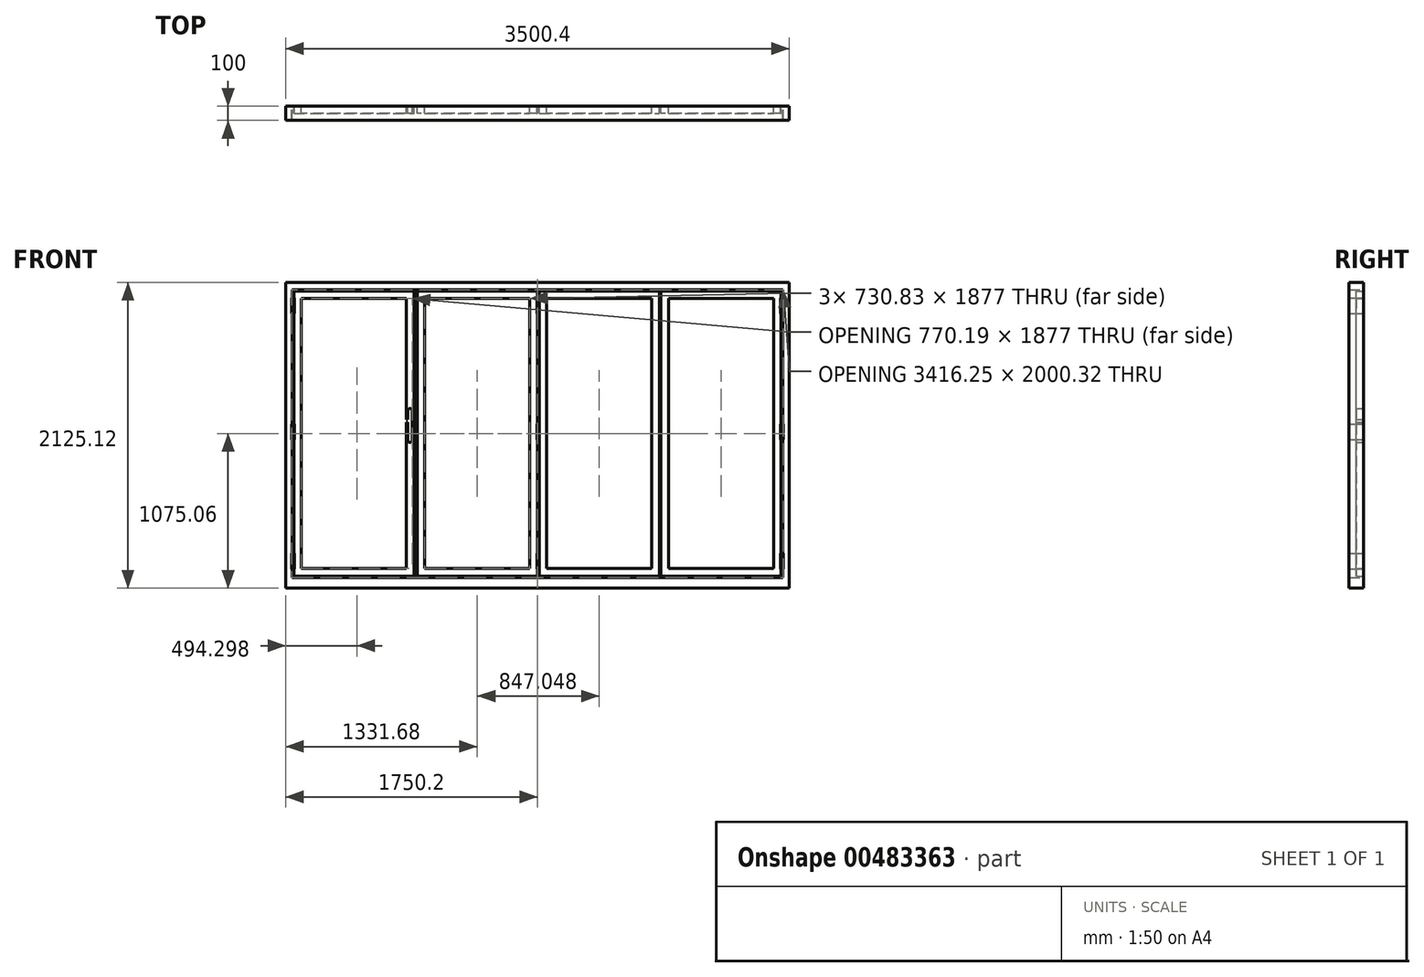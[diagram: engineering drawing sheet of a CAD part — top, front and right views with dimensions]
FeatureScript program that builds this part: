
annotation { "Feature Type Name" : "Feature", "Feature Type Description" : "" }
export const myFeature = defineFeature(function(context is Context, id is Id, definition is map)
    precondition{}
    {
        {
            var Q0;
            Q0=qCreatedBy(makeId("Front.planeOp"),FACE);
            var sketch = newSketch(context, id + "F0", { "sketchPlane" : qUnion([Q0])});
            skLineSegment(sketch, "E0", {"start": v(-1203.5, 497.7) * mm, "end": v(-1203.5, 547.7) * mm});
            skLineSegment(sketch, "E1", {"start": v(-1216.3, 497.7) * mm, "end": v(-1216.3, 547.7) * mm});
            skLineSegment(sketch, "E2", {"start": v(-1216.3, 497.7) * mm, "end": v(-1198.26, 497.7) * mm});
            skLineSegment(sketch, "E3", {"start": v(-1216.3, 547.7) * mm, "end": v(-1198.26, 547.7) * mm});
            skLineSegment(sketch, "E4", {"start": v(-1203.5, 551.7) * mm, "end": v(-1203.5, 601.7) * mm});
            skLineSegment(sketch, "E5", {"start": v(-1216.3, 551.7) * mm, "end": v(-1216.3, 601.7) * mm});
            skLineSegment(sketch, "E6", {"start": v(-1216.3, 551.7) * mm, "end": v(-1198.26, 551.7) * mm});
            skLineSegment(sketch, "E7", {"start": v(-1216.3, 601.7) * mm, "end": v(-1198.26, 601.7) * mm});
            skLineSegment(sketch, "E8", {"start": v(-1198.26, 547.7) * mm, "end": v(-1198.26, 549.7) * mm});
            skLineSegment(sketch, "E9", {"start": v(-1198.26, 549.7) * mm, "end": v(-1216.3, 549.7) * mm});
            skLineSegment(sketch, "E10", {"start": v(-1216.3, 549.7) * mm, "end": v(-1216.3, 547.7) * mm});
            skLineSegment(sketch, "E11", {"start": v(-1198.26, 551.7) * mm, "end": v(-1198.26, 549.7) * mm});
            skLineSegment(sketch, "E12", {"start": v(-1216.3, 549.7) * mm, "end": v(-1216.3, 551.7) * mm});
            skLineSegment(sketch, "E13", {"start": v(-1198.26, 497.7) * mm, "end": v(-1198.26, 495.7) * mm});
            skLineSegment(sketch, "E14", {"start": v(-1198.26, 495.7) * mm, "end": v(-1216.3, 495.7) * mm});
            skLineSegment(sketch, "E15", {"start": v(-1216.3, 495.7) * mm, "end": v(-1216.3, 497.7) * mm});
            skLineSegment(sketch, "E16", {"start": v(-1198.26, 601.7) * mm, "end": v(-1198.26, 603.7) * mm});
            skLineSegment(sketch, "E17", {"start": v(-1198.26, 603.7) * mm, "end": v(-1216.3, 603.7) * mm});
            skLineSegment(sketch, "E18", {"start": v(-1216.3, 603.7) * mm, "end": v(-1216.3, 601.7) * mm});
            skLineSegment(sketch, "E19", {"start": v(487.82, -378.21) * mm, "end": v(487.82, -328.21) * mm});
            skLineSegment(sketch, "E20", {"start": v(500.63, -378.21) * mm, "end": v(500.63, -328.21) * mm});
            skLineSegment(sketch, "E21", {"start": v(505.86, -378.21) * mm, "end": v(487.82, -378.21) * mm});
            skLineSegment(sketch, "E22", {"start": v(505.86, -328.21) * mm, "end": v(487.82, -328.21) * mm});
            skLineSegment(sketch, "E23", {"start": v(487.82, -324.21) * mm, "end": v(487.82, -274.21) * mm});
            skLineSegment(sketch, "E24", {"start": v(500.63, -324.21) * mm, "end": v(500.63, -274.21) * mm});
            skLineSegment(sketch, "E25", {"start": v(505.86, -324.21) * mm, "end": v(487.82, -324.21) * mm});
            skLineSegment(sketch, "E26", {"start": v(505.86, -274.21) * mm, "end": v(487.82, -274.21) * mm});
            skLineSegment(sketch, "E27", {"start": v(487.82, -328.21) * mm, "end": v(487.82, -326.21) * mm});
            skLineSegment(sketch, "E28", {"start": v(487.82, -326.21) * mm, "end": v(505.86, -326.21) * mm});
            skLineSegment(sketch, "E29", {"start": v(505.86, -326.21) * mm, "end": v(505.86, -328.21) * mm});
            skLineSegment(sketch, "E30", {"start": v(487.82, -324.21) * mm, "end": v(487.82, -326.21) * mm});
            skLineSegment(sketch, "E31", {"start": v(505.86, -326.21) * mm, "end": v(505.86, -324.21) * mm});
            skLineSegment(sketch, "E32", {"start": v(487.82, -378.21) * mm, "end": v(487.82, -380.21) * mm});
            skLineSegment(sketch, "E33", {"start": v(487.82, -380.21) * mm, "end": v(505.86, -380.21) * mm});
            skLineSegment(sketch, "E34", {"start": v(505.86, -380.21) * mm, "end": v(505.86, -378.21) * mm});
            skLineSegment(sketch, "E35", {"start": v(487.82, -274.21) * mm, "end": v(487.82, -272.21) * mm});
            skLineSegment(sketch, "E36", {"start": v(487.82, -272.21) * mm, "end": v(505.86, -272.21) * mm});
            skLineSegment(sketch, "E37", {"start": v(505.86, -272.21) * mm, "end": v(505.86, -274.21) * mm});
            skLineSegment(sketch, "E38", {"start": v(487.82, -1175.3) * mm, "end": v(487.82, -1225.3) * mm});
            skLineSegment(sketch, "E39", {"start": v(500.63, -1175.3) * mm, "end": v(500.63, -1225.3) * mm});
            skLineSegment(sketch, "E40", {"start": v(505.86, -1175.3) * mm, "end": v(487.82, -1175.3) * mm});
            skLineSegment(sketch, "E41", {"start": v(505.86, -1225.3) * mm, "end": v(487.82, -1225.3) * mm});
            skLineSegment(sketch, "E42", {"start": v(487.82, -1229.3) * mm, "end": v(487.82, -1279.3) * mm});
            skLineSegment(sketch, "E43", {"start": v(500.63, -1229.3) * mm, "end": v(500.63, -1279.3) * mm});
            skLineSegment(sketch, "E44", {"start": v(505.86, -1229.3) * mm, "end": v(487.82, -1229.3) * mm});
            skLineSegment(sketch, "E45", {"start": v(505.86, -1279.3) * mm, "end": v(487.82, -1279.3) * mm});
            skLineSegment(sketch, "E46", {"start": v(487.82, -1225.3) * mm, "end": v(487.82, -1227.3) * mm});
            skLineSegment(sketch, "E47", {"start": v(487.82, -1227.3) * mm, "end": v(505.86, -1227.3) * mm});
            skLineSegment(sketch, "E48", {"start": v(505.86, -1227.3) * mm, "end": v(505.86, -1225.3) * mm});
            skLineSegment(sketch, "E49", {"start": v(487.82, -1229.3) * mm, "end": v(487.82, -1227.3) * mm});
            skLineSegment(sketch, "E50", {"start": v(505.86, -1227.3) * mm, "end": v(505.86, -1229.3) * mm});
            skLineSegment(sketch, "E51", {"start": v(487.82, -1175.3) * mm, "end": v(487.82, -1173.3) * mm});
            skLineSegment(sketch, "E52", {"start": v(487.82, -1173.3) * mm, "end": v(505.86, -1173.3) * mm});
            skLineSegment(sketch, "E53", {"start": v(505.86, -1173.3) * mm, "end": v(505.86, -1175.3) * mm});
            skLineSegment(sketch, "E54", {"start": v(487.82, -1279.3) * mm, "end": v(487.82, -1281.3) * mm});
            skLineSegment(sketch, "E55", {"start": v(487.82, -1281.3) * mm, "end": v(505.86, -1281.3) * mm});
            skLineSegment(sketch, "E56", {"start": v(505.86, -1281.3) * mm, "end": v(505.86, -1279.3) * mm});
            skLineSegment(sketch, "E57", {"start": v(2181.92, -1175.3) * mm, "end": v(2181.92, -1225.3) * mm});
            skLineSegment(sketch, "E58", {"start": v(2199.95, -1175.3) * mm, "end": v(2199.95, -1225.3) * mm});
            skLineSegment(sketch, "E59", {"start": v(2199.95, -1175.3) * mm, "end": v(2181.92, -1175.3) * mm});
            skLineSegment(sketch, "E60", {"start": v(2199.95, -1225.3) * mm, "end": v(2181.92, -1225.3) * mm});
            skLineSegment(sketch, "E61", {"start": v(2181.92, -1229.3) * mm, "end": v(2181.92, -1279.3) * mm});
            skLineSegment(sketch, "E62", {"start": v(2199.95, -1229.3) * mm, "end": v(2199.95, -1279.3) * mm});
            skLineSegment(sketch, "E63", {"start": v(2199.95, -1229.3) * mm, "end": v(2181.92, -1229.3) * mm});
            skLineSegment(sketch, "E64", {"start": v(2199.95, -1279.3) * mm, "end": v(2181.92, -1279.3) * mm});
            skLineSegment(sketch, "E65", {"start": v(2181.92, -1225.3) * mm, "end": v(2181.92, -1227.3) * mm});
            skLineSegment(sketch, "E66", {"start": v(2181.92, -1227.3) * mm, "end": v(2199.95, -1227.3) * mm});
            skLineSegment(sketch, "E67", {"start": v(2199.95, -1227.3) * mm, "end": v(2199.95, -1225.3) * mm});
            skLineSegment(sketch, "E68", {"start": v(2181.92, -1229.3) * mm, "end": v(2181.92, -1227.3) * mm});
            skLineSegment(sketch, "E69", {"start": v(2199.95, -1227.3) * mm, "end": v(2199.95, -1229.3) * mm});
            skLineSegment(sketch, "E70", {"start": v(2181.92, -1175.3) * mm, "end": v(2181.92, -1173.3) * mm});
            skLineSegment(sketch, "E71", {"start": v(2181.92, -1173.3) * mm, "end": v(2199.95, -1173.3) * mm});
            skLineSegment(sketch, "E72", {"start": v(2199.95, -1173.3) * mm, "end": v(2199.95, -1175.3) * mm});
            skLineSegment(sketch, "E73", {"start": v(2181.92, -1279.3) * mm, "end": v(2181.92, -1281.3) * mm});
            skLineSegment(sketch, "E74", {"start": v(2181.92, -1281.3) * mm, "end": v(2199.95, -1281.3) * mm});
            skLineSegment(sketch, "E75", {"start": v(2199.95, -1281.3) * mm, "end": v(2199.95, -1279.3) * mm});
            skLineSegment(sketch, "E76", {"start": v(2181.92, -378.21) * mm, "end": v(2181.92, -328.21) * mm});
            skLineSegment(sketch, "E77", {"start": v(2199.95, -378.21) * mm, "end": v(2199.95, -328.21) * mm});
            skLineSegment(sketch, "E78", {"start": v(2199.95, -378.21) * mm, "end": v(2181.92, -378.21) * mm});
            skLineSegment(sketch, "E79", {"start": v(2199.95, -328.21) * mm, "end": v(2181.92, -328.21) * mm});
            skLineSegment(sketch, "E80", {"start": v(2181.92, -324.21) * mm, "end": v(2181.92, -274.21) * mm});
            skLineSegment(sketch, "E81", {"start": v(2199.95, -324.21) * mm, "end": v(2199.95, -274.21) * mm});
            skLineSegment(sketch, "E82", {"start": v(2199.95, -324.21) * mm, "end": v(2181.92, -324.21) * mm});
            skLineSegment(sketch, "E83", {"start": v(2199.95, -274.21) * mm, "end": v(2181.92, -274.21) * mm});
            skLineSegment(sketch, "E84", {"start": v(2181.92, -328.21) * mm, "end": v(2181.92, -326.21) * mm});
            skLineSegment(sketch, "E85", {"start": v(2181.92, -326.21) * mm, "end": v(2199.95, -326.21) * mm});
            skLineSegment(sketch, "E86", {"start": v(2199.95, -326.21) * mm, "end": v(2199.95, -328.21) * mm});
            skLineSegment(sketch, "E87", {"start": v(2181.92, -324.21) * mm, "end": v(2181.92, -326.21) * mm});
            skLineSegment(sketch, "E88", {"start": v(2199.95, -326.21) * mm, "end": v(2199.95, -324.21) * mm});
            skLineSegment(sketch, "E89", {"start": v(2181.92, -378.21) * mm, "end": v(2181.92, -380.21) * mm});
            skLineSegment(sketch, "E90", {"start": v(2181.92, -380.21) * mm, "end": v(2199.95, -380.21) * mm});
            skLineSegment(sketch, "E91", {"start": v(2199.95, -380.21) * mm, "end": v(2199.95, -378.21) * mm});
            skLineSegment(sketch, "E92", {"start": v(2181.92, -274.21) * mm, "end": v(2181.92, -272.21) * mm});
            skLineSegment(sketch, "E93", {"start": v(2181.92, -272.21) * mm, "end": v(2199.95, -272.21) * mm});
            skLineSegment(sketch, "E94", {"start": v(2199.95, -272.21) * mm, "end": v(2199.95, -274.21) * mm});
            skLineSegment(sketch, "E95", {"start": v(2181.92, 497.7) * mm, "end": v(2181.92, 547.7) * mm});
            skLineSegment(sketch, "E96", {"start": v(2199.95, 497.7) * mm, "end": v(2199.95, 547.7) * mm});
            skLineSegment(sketch, "E97", {"start": v(2199.95, 497.7) * mm, "end": v(2181.92, 497.7) * mm});
            skLineSegment(sketch, "E98", {"start": v(2199.95, 547.7) * mm, "end": v(2181.92, 547.7) * mm});
            skLineSegment(sketch, "E99", {"start": v(2181.92, 551.7) * mm, "end": v(2181.92, 601.7) * mm});
            skLineSegment(sketch, "E100", {"start": v(2199.95, 551.7) * mm, "end": v(2199.95, 601.7) * mm});
            skLineSegment(sketch, "E101", {"start": v(2199.95, 551.7) * mm, "end": v(2181.92, 551.7) * mm});
            skLineSegment(sketch, "E102", {"start": v(2199.95, 601.7) * mm, "end": v(2181.92, 601.7) * mm});
            skLineSegment(sketch, "E103", {"start": v(2181.92, 547.7) * mm, "end": v(2181.92, 549.7) * mm});
            skLineSegment(sketch, "E104", {"start": v(2181.92, 549.7) * mm, "end": v(2199.95, 549.7) * mm});
            skLineSegment(sketch, "E105", {"start": v(2199.95, 549.7) * mm, "end": v(2199.95, 547.7) * mm});
            skLineSegment(sketch, "E106", {"start": v(2181.92, 551.7) * mm, "end": v(2181.92, 549.7) * mm});
            skLineSegment(sketch, "E107", {"start": v(2199.95, 549.7) * mm, "end": v(2199.95, 551.7) * mm});
            skLineSegment(sketch, "E108", {"start": v(2181.92, 497.7) * mm, "end": v(2181.92, 495.7) * mm});
            skLineSegment(sketch, "E109", {"start": v(2181.92, 495.7) * mm, "end": v(2199.95, 495.7) * mm});
            skLineSegment(sketch, "E110", {"start": v(2199.95, 495.7) * mm, "end": v(2199.95, 497.7) * mm});
            skLineSegment(sketch, "E111", {"start": v(2181.92, 601.7) * mm, "end": v(2181.92, 603.7) * mm});
            skLineSegment(sketch, "E112", {"start": v(2181.92, 603.7) * mm, "end": v(2199.95, 603.7) * mm});
            skLineSegment(sketch, "E113", {"start": v(2199.95, 603.7) * mm, "end": v(2199.95, 601.7) * mm});
            skLineSegment(sketch, "E114", {"start": v(-1203.5, -378.21) * mm, "end": v(-1203.5, -328.21) * mm});
            skLineSegment(sketch, "E115", {"start": v(-1216.3, -378.21) * mm, "end": v(-1216.3, -328.21) * mm});
            skLineSegment(sketch, "E116", {"start": v(-1216.3, -378.21) * mm, "end": v(-1198.26, -378.21) * mm});
            skLineSegment(sketch, "E117", {"start": v(-1216.3, -328.21) * mm, "end": v(-1198.26, -328.21) * mm});
            skLineSegment(sketch, "E118", {"start": v(-1203.5, -324.21) * mm, "end": v(-1203.5, -274.21) * mm});
            skLineSegment(sketch, "E119", {"start": v(-1216.3, -324.21) * mm, "end": v(-1216.3, -274.21) * mm});
            skLineSegment(sketch, "E120", {"start": v(-1216.3, -324.21) * mm, "end": v(-1198.26, -324.21) * mm});
            skLineSegment(sketch, "E121", {"start": v(-1216.3, -274.21) * mm, "end": v(-1198.26, -274.21) * mm});
            skLineSegment(sketch, "E122", {"start": v(-1198.26, -328.21) * mm, "end": v(-1198.26, -326.21) * mm});
            skLineSegment(sketch, "E123", {"start": v(-1198.26, -326.21) * mm, "end": v(-1216.3, -326.21) * mm});
            skLineSegment(sketch, "E124", {"start": v(-1216.3, -326.21) * mm, "end": v(-1216.3, -328.21) * mm});
            skLineSegment(sketch, "E125", {"start": v(-1198.26, -324.21) * mm, "end": v(-1198.26, -326.21) * mm});
            skLineSegment(sketch, "E126", {"start": v(-1216.3, -326.21) * mm, "end": v(-1216.3, -324.21) * mm});
            skLineSegment(sketch, "E127", {"start": v(-1198.26, -378.21) * mm, "end": v(-1198.26, -380.21) * mm});
            skLineSegment(sketch, "E128", {"start": v(-1198.26, -380.21) * mm, "end": v(-1216.3, -380.21) * mm});
            skLineSegment(sketch, "E129", {"start": v(-1216.3, -380.21) * mm, "end": v(-1216.3, -378.21) * mm});
            skLineSegment(sketch, "E130", {"start": v(-1198.26, -274.21) * mm, "end": v(-1198.26, -272.21) * mm});
            skLineSegment(sketch, "E131", {"start": v(-1198.26, -272.21) * mm, "end": v(-1216.3, -272.21) * mm});
            skLineSegment(sketch, "E132", {"start": v(-1216.3, -272.21) * mm, "end": v(-1216.3, -274.21) * mm});
            skLineSegment(sketch, "E133", {"start": v(-1203.5, -1175.3) * mm, "end": v(-1203.5, -1225.3) * mm});
            skLineSegment(sketch, "E134", {"start": v(-1216.3, -1175.3) * mm, "end": v(-1216.3, -1225.3) * mm});
            skLineSegment(sketch, "E135", {"start": v(-1216.3, -1175.3) * mm, "end": v(-1198.26, -1175.3) * mm});
            skLineSegment(sketch, "E136", {"start": v(-1216.3, -1225.3) * mm, "end": v(-1198.26, -1225.3) * mm});
            skLineSegment(sketch, "E137", {"start": v(-1203.5, -1229.3) * mm, "end": v(-1203.5, -1279.3) * mm});
            skLineSegment(sketch, "E138", {"start": v(-1216.3, -1229.3) * mm, "end": v(-1216.3, -1279.3) * mm});
            skLineSegment(sketch, "E139", {"start": v(-1216.3, -1229.3) * mm, "end": v(-1198.26, -1229.3) * mm});
            skLineSegment(sketch, "E140", {"start": v(-1216.3, -1279.3) * mm, "end": v(-1198.26, -1279.3) * mm});
            skLineSegment(sketch, "E141", {"start": v(-1198.26, -1225.3) * mm, "end": v(-1198.26, -1227.3) * mm});
            skLineSegment(sketch, "E142", {"start": v(-1198.26, -1227.3) * mm, "end": v(-1216.3, -1227.3) * mm});
            skLineSegment(sketch, "E143", {"start": v(-1216.3, -1227.3) * mm, "end": v(-1216.3, -1225.3) * mm});
            skLineSegment(sketch, "E144", {"start": v(-1198.26, -1229.3) * mm, "end": v(-1198.26, -1227.3) * mm});
            skLineSegment(sketch, "E145", {"start": v(-1216.3, -1227.3) * mm, "end": v(-1216.3, -1229.3) * mm});
            skLineSegment(sketch, "E146", {"start": v(-1198.26, -1175.3) * mm, "end": v(-1198.26, -1173.3) * mm});
            skLineSegment(sketch, "E147", {"start": v(-1198.26, -1173.3) * mm, "end": v(-1216.3, -1173.3) * mm});
            skLineSegment(sketch, "E148", {"start": v(-1216.3, -1173.3) * mm, "end": v(-1216.3, -1175.3) * mm});
            skLineSegment(sketch, "E149", {"start": v(-1198.26, -1279.3) * mm, "end": v(-1198.26, -1281.3) * mm});
            skLineSegment(sketch, "E150", {"start": v(-1198.26, -1281.3) * mm, "end": v(-1216.3, -1281.3) * mm});
            skLineSegment(sketch, "E151", {"start": v(-1216.3, -1281.3) * mm, "end": v(-1216.3, -1279.3) * mm});
            skLineSegment(sketch, "E152", {"start": v(487.82, 497.7) * mm, "end": v(487.82, 547.7) * mm});
            skLineSegment(sketch, "E153", {"start": v(500.63, 497.7) * mm, "end": v(500.63, 547.7) * mm});
            skLineSegment(sketch, "E154", {"start": v(505.86, 497.7) * mm, "end": v(487.82, 497.7) * mm});
            skLineSegment(sketch, "E155", {"start": v(505.86, 547.7) * mm, "end": v(487.82, 547.7) * mm});
            skLineSegment(sketch, "E156", {"start": v(487.82, 551.7) * mm, "end": v(487.82, 601.7) * mm});
            skLineSegment(sketch, "E157", {"start": v(500.63, 551.7) * mm, "end": v(500.63, 601.7) * mm});
            skLineSegment(sketch, "E158", {"start": v(505.86, 551.7) * mm, "end": v(487.82, 551.7) * mm});
            skLineSegment(sketch, "E159", {"start": v(505.86, 601.7) * mm, "end": v(487.82, 601.7) * mm});
            skLineSegment(sketch, "E160", {"start": v(487.82, 547.7) * mm, "end": v(487.82, 549.7) * mm});
            skLineSegment(sketch, "E161", {"start": v(487.82, 549.7) * mm, "end": v(505.86, 549.7) * mm});
            skLineSegment(sketch, "E162", {"start": v(505.86, 549.7) * mm, "end": v(505.86, 547.7) * mm});
            skLineSegment(sketch, "E163", {"start": v(487.82, 551.7) * mm, "end": v(487.82, 549.7) * mm});
            skLineSegment(sketch, "E164", {"start": v(505.86, 549.7) * mm, "end": v(505.86, 551.7) * mm});
            skLineSegment(sketch, "E165", {"start": v(487.82, 497.7) * mm, "end": v(487.82, 495.7) * mm});
            skLineSegment(sketch, "E166", {"start": v(487.82, 495.7) * mm, "end": v(505.86, 495.7) * mm});
            skLineSegment(sketch, "E167", {"start": v(505.86, 495.7) * mm, "end": v(505.86, 497.7) * mm});
            skLineSegment(sketch, "E168", {"start": v(487.82, 601.7) * mm, "end": v(487.82, 603.7) * mm});
            skLineSegment(sketch, "E169", {"start": v(487.82, 603.7) * mm, "end": v(505.86, 603.7) * mm});
            skLineSegment(sketch, "E170", {"start": v(505.86, 603.7) * mm, "end": v(505.86, 601.7) * mm});
            skLineSegment(sketch, "E171", {"start": v(2196.94, -380.21) * mm, "end": v(2196.94, -1173.3) * mm});
            skLineSegment(sketch, "E172", {"start": v(2242.03, -1329.3) * mm, "end": v(2242.03, -1017.31) * mm});
            skLineSegment(sketch, "E173", {"start": v(2196.94, -1329.3) * mm, "end": v(2196.94, -1338.95) * mm});
            skLineSegment(sketch, "E174", {"start": v(-344.2, -1329.3) * mm, "end": v(-363.24, -1329.3) * mm});
            skLineSegment(sketch, "E175", {"start": v(-1137.64, -1265.8) * mm, "end": v(-429.86, -1265.8) * mm});
            skLineSegment(sketch, "E176", {"start": v(-1124.75, -1252.92) * mm, "end": v(-1201.27, -1329.3) * mm});
            skLineSegment(sketch, "E177", {"start": v(-1201.27, -380.21) * mm, "end": v(-1201.27, -1173.3) * mm});
            skLineSegment(sketch, "E178", {"start": v(-1213.29, -1281.3) * mm, "end": v(-1213.29, -1329.3) * mm});
            skLineSegment(sketch, "E179", {"start": v(-1213.29, -380.21) * mm, "end": v(-1213.29, -1173.3) * mm});
            skLineSegment(sketch, "E180", {"start": v(-1201.27, -1281.3) * mm, "end": v(-1201.27, -1329.3) * mm});
            skLineSegment(sketch, "E181", {"start": v(-1201.27, -1329.3) * mm, "end": v(-366.24, -1329.3) * mm});
            skLineSegment(sketch, "E182", {"start": v(-418.34, -1277.3) * mm, "end": v(-1149.17, -1277.3) * mm});
            skLineSegment(sketch, "E183", {"start": v(-438.73, -1256.94) * mm, "end": v(-1128.77, -1256.94) * mm});
            skLineSegment(sketch, "E184", {"start": v(-442.76, -1252.92) * mm, "end": v(-366.24, -1329.3) * mm});
            skLineSegment(sketch, "E185", {"start": v(-366.24, -1017.31) * mm, "end": v(-366.24, -1329.3) * mm});
            skLineSegment(sketch, "E186", {"start": v(-442.76, -1252.92) * mm, "end": v(-1124.75, -1252.92) * mm});
            skLineSegment(sketch, "E187", {"start": v(-1258.37, -1388.85) * mm, "end": v(-1258.37, -1338.95) * mm});
            skLineSegment(sketch, "E188", {"start": v(-1213.29, -1329.3) * mm, "end": v(-1213.29, -1338.95) * mm});
            skLineSegment(sketch, "E189", {"start": v(2196.94, -272.21) * mm, "end": v(2196.94, 495.7) * mm});
            skLineSegment(sketch, "E190", {"start": v(2242.03, 651.7) * mm, "end": v(2242.03, -1084.15) * mm});
            skLineSegment(sketch, "E191", {"start": v(2196.94, 651.7) * mm, "end": v(2196.94, 661.36) * mm});
            skLineSegment(sketch, "E192", {"start": v(-363.24, 651.7) * mm, "end": v(-363.24, -1329.3) * mm});
            skLineSegment(sketch, "E193", {"start": v(-344.2, 651.7) * mm, "end": v(-363.24, 651.7) * mm});
            skLineSegment(sketch, "E194", {"start": v(-1149.17, -1277.3) * mm, "end": v(-1149.17, 599.7) * mm});
            skLineSegment(sketch, "E195", {"start": v(-1137.64, -1265.8) * mm, "end": v(-1137.64, 588.2) * mm});
            skLineSegment(sketch, "E196", {"start": v(-1128.77, -1256.94) * mm, "end": v(-1128.77, 579.35) * mm});
            skLineSegment(sketch, "E197", {"start": v(-1124.75, 575.34) * mm, "end": v(-1201.27, 651.7) * mm});
            skLineSegment(sketch, "E198", {"start": v(-1201.27, -272.21) * mm, "end": v(-1201.27, 495.7) * mm});
            skLineSegment(sketch, "E199", {"start": v(-1213.29, 603.7) * mm, "end": v(-1213.29, 651.7) * mm});
            skLineSegment(sketch, "E200", {"start": v(-1213.29, -272.21) * mm, "end": v(-1213.29, 495.7) * mm});
            skLineSegment(sketch, "E201", {"start": v(-1124.75, -1252.92) * mm, "end": v(-1124.75, 575.34) * mm});
            skLineSegment(sketch, "E202", {"start": v(-1201.27, 603.7) * mm, "end": v(-1201.27, 651.7) * mm});
            skLineSegment(sketch, "E203", {"start": v(-1201.27, 651.7) * mm, "end": v(-366.24, 651.7) * mm});
            skLineSegment(sketch, "E204", {"start": v(-418.34, 599.7) * mm, "end": v(-1149.17, 599.7) * mm});
            skLineSegment(sketch, "E205", {"start": v(-429.86, 588.2) * mm, "end": v(-1137.64, 588.2) * mm});
            skLineSegment(sketch, "E206", {"start": v(-438.73, 579.35) * mm, "end": v(-1128.77, 579.35) * mm});
            skLineSegment(sketch, "E207", {"start": v(-442.76, 575.34) * mm, "end": v(-366.24, 651.7) * mm});
            skLineSegment(sketch, "E208", {"start": v(-366.24, -1084.15) * mm, "end": v(-366.24, 651.7) * mm});
            skLineSegment(sketch, "E209", {"start": v(-442.76, 575.34) * mm, "end": v(-1124.75, 575.34) * mm});
            skLineSegment(sketch, "E210", {"start": v(-1213.29, 651.7) * mm, "end": v(-1213.29, 661.36) * mm});
            skArc(sketch, "E211", {"start": v(-385.44, -247.83) * mm, "mid": v(-386.91, -244.3) * mm, "end": v(-390.45, -242.83) * mm});
            skLineSegment(sketch, "E212", {"start": v(-390.45, -242.83) * mm, "end": v(-497.12, -242.83) * mm});
            skArc(sketch, "E213", {"start": v(-497.12, -242.83) * mm, "mid": v(-504.2, -245.75) * mm, "end": v(-507.14, -252.83) * mm});
            skLineSegment(sketch, "E214", {"start": v(-507.14, -252.83) * mm, "end": v(-507.14, -251.52) * mm});
            skArc(sketch, "E215", {"start": v(-507.14, -251.52) * mm, "mid": v(-504.2, -258.6) * mm, "end": v(-497.12, -261.52) * mm});
            skLineSegment(sketch, "E216", {"start": v(-497.12, -261.52) * mm, "end": v(-390.45, -261.52) * mm});
            skArc(sketch, "E217", {"start": v(-390.45, -261.52) * mm, "mid": v(-386.91, -260.06) * mm, "end": v(-385.44, -256.52) * mm});
            skLineSegment(sketch, "E218", {"start": v(-385.44, -256.52) * mm, "end": v(-385.44, -247.83) * mm});
            skLineSegment(sketch, "E219", {"start": v(-410.04, -261.52) * mm, "end": v(-410.04, -385.57) * mm});
            skArc(sketch, "E220", {"start": v(-410.04, -385.57) * mm, "mid": v(-405.48, -396.54) * mm, "end": v(-394.5, -401.07) * mm});
            skArc(sketch, "E221", {"start": v(-394.5, -401.07) * mm, "mid": v(-383.53, -396.54) * mm, "end": v(-378.98, -385.57) * mm});
            skLineSegment(sketch, "E222", {"start": v(-378.98, -385.57) * mm, "end": v(-378.98, -181.57) * mm});
            skArc(sketch, "E223", {"start": v(-378.98, -181.57) * mm, "mid": v(-383.53, -170.6) * mm, "end": v(-394.5, -166.07) * mm});
            skArc(sketch, "E224", {"start": v(-394.5, -166.07) * mm, "mid": v(-405.48, -170.6) * mm, "end": v(-410.04, -181.57) * mm});
            skLineSegment(sketch, "E225", {"start": v(-410.04, -181.57) * mm, "end": v(-410.04, -242.83) * mm});
            skLineSegment(sketch, "E226", {"start": v(-399.52, -349.8) * mm, "end": v(-399.52, -361.78) * mm});
            skLineSegment(sketch, "E227", {"start": v(-389.5, -361.78) * mm, "end": v(-389.5, -349.8) * mm});
            skLineSegment(sketch, "E228", {"start": v(-442.76, -1252.92) * mm, "end": v(-442.76, -261.52) * mm});
            skLineSegment(sketch, "E229", {"start": v(-442.76, -242.83) * mm, "end": v(-442.76, 575.34) * mm});
            skLineSegment(sketch, "E230", {"start": v(-438.73, -242.83) * mm, "end": v(-438.73, 579.35) * mm});
            skLineSegment(sketch, "E231", {"start": v(-438.73, -1256.94) * mm, "end": v(-438.73, -261.52) * mm});
            skLineSegment(sketch, "E232", {"start": v(-429.86, -242.83) * mm, "end": v(-429.86, 588.2) * mm});
            skLineSegment(sketch, "E233", {"start": v(-429.86, -1265.8) * mm, "end": v(-429.86, -261.52) * mm});
            skLineSegment(sketch, "E234", {"start": v(-418.34, -242.83) * mm, "end": v(-418.34, 599.7) * mm});
            skLineSegment(sketch, "E235", {"start": v(-418.34, -1277.3) * mm, "end": v(-418.34, -261.52) * mm});
            skArc(sketch, "E236", {"start": v(-399.52, -361.78) * mm, "mid": v(-398.05, -365.32) * mm, "end": v(-394.5, -366.79) * mm});
            skArc(sketch, "E237", {"start": v(-394.5, -366.79) * mm, "mid": v(-390.97, -365.32) * mm, "end": v(-389.5, -361.78) * mm});
            skArc(sketch, "E238", {"start": v(-389.5, -349.82) * mm, "mid": v(-394.5, -334.42) * mm, "end": v(-399.52, -349.82) * mm});
            skLineSegment(sketch, "E239", {"start": v(427.2, -1265.8) * mm, "end": v(-280.58, -1265.8) * mm});
            skLineSegment(sketch, "E240", {"start": v(414.3, -1252.92) * mm, "end": v(490.83, -1329.3) * mm});
            skLineSegment(sketch, "E241", {"start": v(490.83, -380.21) * mm, "end": v(490.83, -1173.3) * mm});
            skLineSegment(sketch, "E242", {"start": v(490.83, -1281.3) * mm, "end": v(490.83, -1329.3) * mm});
            skLineSegment(sketch, "E243", {"start": v(490.83, -1329.3) * mm, "end": v(-344.2, -1329.3) * mm});
            skLineSegment(sketch, "E244", {"start": v(-292.1, -1277.3) * mm, "end": v(438.73, -1277.3) * mm});
            skLineSegment(sketch, "E245", {"start": v(-271.7, -1256.94) * mm, "end": v(418.33, -1256.94) * mm});
            skLineSegment(sketch, "E246", {"start": v(-267.68, -1252.92) * mm, "end": v(-344.2, -1329.3) * mm});
            skLineSegment(sketch, "E247", {"start": v(-344.2, -1017.31) * mm, "end": v(-344.2, -1173.3) * mm});
            skLineSegment(sketch, "E248", {"start": v(-267.68, -1252.92) * mm, "end": v(414.3, -1252.92) * mm});
            skLineSegment(sketch, "E249", {"start": v(438.73, -1277.3) * mm, "end": v(438.73, 599.7) * mm});
            skLineSegment(sketch, "E250", {"start": v(427.2, -1265.8) * mm, "end": v(427.2, 588.2) * mm});
            skLineSegment(sketch, "E251", {"start": v(418.33, -1256.94) * mm, "end": v(418.33, 579.35) * mm});
            skLineSegment(sketch, "E252", {"start": v(414.3, 575.34) * mm, "end": v(490.83, 651.7) * mm});
            skLineSegment(sketch, "E253", {"start": v(490.83, -272.21) * mm, "end": v(490.83, 495.7) * mm});
            skLineSegment(sketch, "E254", {"start": v(414.3, -1252.92) * mm, "end": v(414.3, 575.34) * mm});
            skLineSegment(sketch, "E255", {"start": v(490.83, 603.7) * mm, "end": v(490.83, 651.7) * mm});
            skLineSegment(sketch, "E256", {"start": v(490.83, 651.7) * mm, "end": v(-344.2, 651.7) * mm});
            skLineSegment(sketch, "E257", {"start": v(-292.1, 599.7) * mm, "end": v(438.73, 599.7) * mm});
            skLineSegment(sketch, "E258", {"start": v(-280.58, 588.2) * mm, "end": v(427.2, 588.2) * mm});
            skLineSegment(sketch, "E259", {"start": v(-271.7, 579.35) * mm, "end": v(418.33, 579.35) * mm});
            skLineSegment(sketch, "E260", {"start": v(-267.68, 575.34) * mm, "end": v(-344.2, 651.7) * mm});
            skLineSegment(sketch, "E261", {"start": v(-344.2, -1329.3) * mm, "end": v(-344.2, 651.7) * mm});
            skLineSegment(sketch, "E262", {"start": v(-267.68, 575.34) * mm, "end": v(414.3, 575.34) * mm});
            skLineSegment(sketch, "E263", {"start": v(-267.68, -1252.92) * mm, "end": v(-267.68, 575.34) * mm});
            skLineSegment(sketch, "E264", {"start": v(-271.7, -1256.94) * mm, "end": v(-271.7, 579.35) * mm});
            skLineSegment(sketch, "E265", {"start": v(-280.58, -1265.8) * mm, "end": v(-280.58, 588.2) * mm});
            skLineSegment(sketch, "E266", {"start": v(-292.1, -1277.3) * mm, "end": v(-292.1, 599.7) * mm});
            skLineSegment(sketch, "E267", {"start": v(566.47, -1265.8) * mm, "end": v(1274.25, -1265.8) * mm});
            skLineSegment(sketch, "E268", {"start": v(579.37, -1252.92) * mm, "end": v(502.85, -1329.3) * mm});
            skLineSegment(sketch, "E269", {"start": v(502.85, -380.21) * mm, "end": v(502.85, -1173.3) * mm});
            skLineSegment(sketch, "E270", {"start": v(502.85, -1281.3) * mm, "end": v(502.85, -1329.3) * mm});
            skLineSegment(sketch, "E271", {"start": v(502.85, -1329.3) * mm, "end": v(1337.87, -1329.3) * mm});
            skLineSegment(sketch, "E272", {"start": v(1285.77, -1277.3) * mm, "end": v(554.95, -1277.3) * mm});
            skLineSegment(sketch, "E273", {"start": v(1265.38, -1256.94) * mm, "end": v(575.34, -1256.94) * mm});
            skLineSegment(sketch, "E274", {"start": v(1261.36, -1252.92) * mm, "end": v(1337.87, -1329.3) * mm});
            skLineSegment(sketch, "E275", {"start": v(1337.87, -1017.31) * mm, "end": v(1337.87, -1173.3) * mm});
            skLineSegment(sketch, "E276", {"start": v(1261.36, -1252.92) * mm, "end": v(579.37, -1252.92) * mm});
            skLineSegment(sketch, "E277", {"start": v(554.95, -1277.3) * mm, "end": v(554.95, 599.7) * mm});
            skLineSegment(sketch, "E278", {"start": v(566.47, -1265.8) * mm, "end": v(566.47, 588.2) * mm});
            skLineSegment(sketch, "E279", {"start": v(575.34, -1256.94) * mm, "end": v(575.34, 579.35) * mm});
            skLineSegment(sketch, "E280", {"start": v(579.37, 575.34) * mm, "end": v(502.85, 651.7) * mm});
            skLineSegment(sketch, "E281", {"start": v(502.85, -272.21) * mm, "end": v(502.85, 495.7) * mm});
            skLineSegment(sketch, "E282", {"start": v(579.37, -1252.92) * mm, "end": v(579.37, 575.34) * mm});
            skLineSegment(sketch, "E283", {"start": v(502.85, 603.7) * mm, "end": v(502.85, 651.7) * mm});
            skLineSegment(sketch, "E284", {"start": v(502.85, 651.7) * mm, "end": v(1337.87, 651.7) * mm});
            skLineSegment(sketch, "E285", {"start": v(1285.77, 599.7) * mm, "end": v(554.95, 599.7) * mm});
            skLineSegment(sketch, "E286", {"start": v(1274.25, 588.2) * mm, "end": v(566.47, 588.2) * mm});
            skLineSegment(sketch, "E287", {"start": v(1265.38, 579.35) * mm, "end": v(575.34, 579.35) * mm});
            skLineSegment(sketch, "E288", {"start": v(1261.36, 575.34) * mm, "end": v(1337.87, 651.7) * mm});
            skLineSegment(sketch, "E289", {"start": v(1337.87, -1329.3) * mm, "end": v(1337.87, 651.7) * mm});
            skLineSegment(sketch, "E290", {"start": v(1261.36, 575.34) * mm, "end": v(579.37, 575.34) * mm});
            skLineSegment(sketch, "E291", {"start": v(1261.36, -1252.92) * mm, "end": v(1261.36, 575.34) * mm});
            skLineSegment(sketch, "E292", {"start": v(1265.38, -1256.94) * mm, "end": v(1265.38, 579.35) * mm});
            skLineSegment(sketch, "E293", {"start": v(1274.25, -1265.8) * mm, "end": v(1274.25, 588.2) * mm});
            skLineSegment(sketch, "E294", {"start": v(1285.77, -1277.3) * mm, "end": v(1285.77, 599.7) * mm});
            skLineSegment(sketch, "E295", {"start": v(2121.3, -1265.8) * mm, "end": v(1413.52, -1265.8) * mm});
            skLineSegment(sketch, "E296", {"start": v(2108.4, -1252.92) * mm, "end": v(2184.92, -1329.3) * mm});
            skLineSegment(sketch, "E297", {"start": v(2184.92, -380.21) * mm, "end": v(2184.92, -1173.3) * mm});
            skLineSegment(sketch, "E298", {"start": v(2184.92, -1281.3) * mm, "end": v(2184.92, -1329.3) * mm});
            skLineSegment(sketch, "E299", {"start": v(2184.92, -1329.3) * mm, "end": v(1349.9, -1329.3) * mm});
            skLineSegment(sketch, "E300", {"start": v(1402, -1277.3) * mm, "end": v(2132.82, -1277.3) * mm});
            skLineSegment(sketch, "E301", {"start": v(1422.39, -1256.94) * mm, "end": v(2112.43, -1256.94) * mm});
            skLineSegment(sketch, "E302", {"start": v(1426.41, -1252.92) * mm, "end": v(1349.9, -1329.3) * mm});
            skLineSegment(sketch, "E303", {"start": v(1349.9, -1017.31) * mm, "end": v(1349.9, -1173.3) * mm});
            skLineSegment(sketch, "E304", {"start": v(1426.41, -1252.92) * mm, "end": v(2108.4, -1252.92) * mm});
            skLineSegment(sketch, "E305", {"start": v(2132.82, -1277.3) * mm, "end": v(2132.82, 599.7) * mm});
            skLineSegment(sketch, "E306", {"start": v(2121.3, -1265.8) * mm, "end": v(2121.3, 588.2) * mm});
            skLineSegment(sketch, "E307", {"start": v(2112.43, -1256.94) * mm, "end": v(2112.43, 579.35) * mm});
            skLineSegment(sketch, "E308", {"start": v(2108.4, 575.34) * mm, "end": v(2184.92, 651.7) * mm});
            skLineSegment(sketch, "E309", {"start": v(2184.92, -272.21) * mm, "end": v(2184.92, 495.7) * mm});
            skLineSegment(sketch, "E310", {"start": v(2108.4, -1252.92) * mm, "end": v(2108.4, 575.34) * mm});
            skLineSegment(sketch, "E311", {"start": v(2184.92, 603.7) * mm, "end": v(2184.92, 651.7) * mm});
            skLineSegment(sketch, "E312", {"start": v(2184.92, 651.7) * mm, "end": v(1349.9, 651.7) * mm});
            skLineSegment(sketch, "E313", {"start": v(1402, 599.7) * mm, "end": v(2132.82, 599.7) * mm});
            skLineSegment(sketch, "E314", {"start": v(1413.52, 588.2) * mm, "end": v(2121.3, 588.2) * mm});
            skLineSegment(sketch, "E315", {"start": v(1422.39, 579.35) * mm, "end": v(2112.43, 579.35) * mm});
            skLineSegment(sketch, "E316", {"start": v(1426.41, 575.34) * mm, "end": v(1349.9, 651.7) * mm});
            skLineSegment(sketch, "E317", {"start": v(1349.9, -1329.3) * mm, "end": v(1349.9, 651.7) * mm});
            skLineSegment(sketch, "E318", {"start": v(1426.41, 575.34) * mm, "end": v(2108.4, 575.34) * mm});
            skLineSegment(sketch, "E319", {"start": v(1426.41, -1252.92) * mm, "end": v(1426.41, 575.34) * mm});
            skLineSegment(sketch, "E320", {"start": v(1422.39, -1256.94) * mm, "end": v(1422.39, 579.35) * mm});
            skLineSegment(sketch, "E321", {"start": v(1413.52, -1265.8) * mm, "end": v(1413.52, 588.2) * mm});
            skLineSegment(sketch, "E322", {"start": v(1402, -1277.3) * mm, "end": v(1402, 599.7) * mm});
            skLineSegment(sketch, "E323", {"start": v(-1258.37, 651.7) * mm, "end": v(-1258.37, 661.36) * mm});
            skLineSegment(sketch, "E324", {"start": v(-1213.29, 651.7) * mm, "end": v(-1258.37, 651.7) * mm});
            skLineSegment(sketch, "E325", {"start": v(-1258.37, 651.7) * mm, "end": v(-1258.37, -1329.3) * mm});
            skLineSegment(sketch, "E326", {"start": v(-1258.37, -1329.3) * mm, "end": v(-1213.29, -1329.3) * mm});
            skLineSegment(sketch, "E327", {"start": v(-1213.29, -1329.3) * mm, "end": v(-1213.29, -1281.3) * mm});
            skLineSegment(sketch, "E328", {"start": v(-1258.37, -1338.95) * mm, "end": v(-1258.37, -1329.3) * mm});
            skLineSegment(sketch, "E329", {"start": v(2242.03, -1329.3) * mm, "end": v(2242.03, -1338.95) * mm});
            skLineSegment(sketch, "E330", {"start": v(-1258.37, -1388.85) * mm, "end": v(2242.03, -1388.85) * mm});
            skLineSegment(sketch, "E331", {"start": v(2242.03, -1388.85) * mm, "end": v(2242.03, -1338.95) * mm});
            skLineSegment(sketch, "E332", {"start": v(2242.03, -1338.95) * mm, "end": v(-1258.37, -1338.95) * mm});
            skLineSegment(sketch, "E333", {"start": v(2242.03, 651.7) * mm, "end": v(2242.03, 661.36) * mm});
            skLineSegment(sketch, "E334", {"start": v(2196.94, -1281.3) * mm, "end": v(2196.94, -1329.3) * mm});
            skLineSegment(sketch, "E335", {"start": v(2196.94, -1329.3) * mm, "end": v(2242.03, -1329.3) * mm});
            skLineSegment(sketch, "E336", {"start": v(2242.03, -1329.3) * mm, "end": v(2242.03, 651.7) * mm});
            skLineSegment(sketch, "E337", {"start": v(2242.03, 651.7) * mm, "end": v(2196.94, 651.7) * mm});
            skLineSegment(sketch, "E338", {"start": v(2196.94, 651.7) * mm, "end": v(2196.94, 603.7) * mm});
            skLineSegment(sketch, "E339", {"start": v(-1258.37, 661.36) * mm, "end": v(2242.03, 661.36) * mm});
            skLineSegment(sketch, "E340", {"start": v(2242.03, 661.36) * mm, "end": v(2242.03, 711.27) * mm});
            skLineSegment(sketch, "E341", {"start": v(2242.03, 711.27) * mm, "end": v(-1258.37, 711.27) * mm});
            skLineSegment(sketch, "E342", {"start": v(-1258.37, 711.27) * mm, "end": v(-1258.37, 661.36) * mm});
            skLineSegment(sketch, "E343", {"start": v(-1198.26, 497.7) * mm, "end": v(-1198.26, 547.7) * mm});
            skLineSegment(sketch, "E344", {"start": v(-1198.26, 551.7) * mm, "end": v(-1198.26, 601.7) * mm});
            skLineSegment(sketch, "E345", {"start": v(-1198.26, -378.21) * mm, "end": v(-1198.26, -328.21) * mm});
            skLineSegment(sketch, "E346", {"start": v(-1198.26, -324.21) * mm, "end": v(-1198.26, -274.21) * mm});
            skLineSegment(sketch, "E347", {"start": v(-1198.26, -1175.3) * mm, "end": v(-1198.26, -1225.3) * mm});
            skLineSegment(sketch, "E348", {"start": v(-1198.26, -1229.3) * mm, "end": v(-1198.26, -1279.3) * mm});
            skLineSegment(sketch, "E349", {"start": v(505.86, 497.7) * mm, "end": v(505.86, 547.7) * mm});
            skLineSegment(sketch, "E350", {"start": v(505.86, 551.7) * mm, "end": v(505.86, 601.7) * mm});
            skLineSegment(sketch, "E351", {"start": v(505.86, -378.21) * mm, "end": v(505.86, -328.21) * mm});
            skLineSegment(sketch, "E352", {"start": v(505.86, -324.21) * mm, "end": v(505.86, -274.21) * mm});
            skLineSegment(sketch, "E353", {"start": v(505.86, -1175.3) * mm, "end": v(505.86, -1225.3) * mm});
            skLineSegment(sketch, "E354", {"start": v(505.86, -1229.3) * mm, "end": v(505.86, -1279.3) * mm});
            skLineSegment(sketch, "E355", {"start": v(2242.03, -1388.85) * mm, "end": v(2242.03, -1413.85) * mm});
            skLineSegment(sketch, "E356", {"start": v(2242.03, -1413.85) * mm, "end": v(-1258.37, -1413.85) * mm});
            skLineSegment(sketch, "E357", {"start": v(-1258.37, -1413.85) * mm, "end": v(-1258.37, -1388.85) * mm});
            skSolve(sketch);
        }
        {
            var Q0;
            Q0 = qSketchRegion(id + "F0", true);
            extrude(context, id + "F1", {"entities" : qUnion([Q0]), "depth" : 100 * mm});
        }
        {
            var Q0;
            {var subQ10=sQuery(id+"F0.wireOp",EDGE,"E177");Q0=makeQuery(id+"F0.imprint","IMPRINT",FACE,{"disambiguationData":[TD([[makeQuery(id+"F0.imprint","IMPRINT",EDGE,{"derivedFrom":subQ10}),1.0]])]});}
            var Q1;
            {var subQ2=sQuery(id+"F0.wireOp",EDGE,"E203");Q1=makeQuery(id+"F0.imprint","IMPRINT",FACE,{"disambiguationData":[TD([[makeQuery(id+"F0.imprint","IMPRINT",EDGE,{"derivedFrom":subQ2}),-1.0]])]});}
            var Q2;
            {var subQ7=sQuery(id+"F0.wireOp",EDGE,"E185");Q2=makeQuery(id+"F0.imprint","IMPRINT",FACE,{"disambiguationData":[TD([[makeQuery(id+"F0.imprint","IMPRINT",EDGE,{"derivedFrom":subQ7}),-1.0]])]});}
            var Q3;
            {var subQ5=sQuery(id+"F0.wireOp",EDGE,"E266");Q3=makeQuery(id+"F0.imprint","IMPRINT",FACE,{"disambiguationData":[TD([[makeQuery(id+"F0.imprint","IMPRINT",EDGE,{"derivedFrom":subQ5}),1.0]])]});}
            var Q4;
            {var subQ2=sQuery(id+"F0.wireOp",EDGE,"E256");Q4=makeQuery(id+"F0.imprint","IMPRINT",FACE,{"disambiguationData":[TD([[makeQuery(id+"F0.imprint","IMPRINT",EDGE,{"derivedFrom":subQ2}),1.0]])]});}
            var Q5;
            {var subQ7=sQuery(id+"F0.wireOp",EDGE,"E241");Q5=makeQuery(id+"F0.imprint","IMPRINT",FACE,{"disambiguationData":[TD([[makeQuery(id+"F0.imprint","IMPRINT",EDGE,{"derivedFrom":subQ7}),-1.0]])]});}
            var Q6;
            {var subQ8=sQuery(id+"F0.wireOp",EDGE,"E269");Q6=makeQuery(id+"F0.imprint","IMPRINT",FACE,{"disambiguationData":[TD([[makeQuery(id+"F0.imprint","IMPRINT",EDGE,{"derivedFrom":subQ8}),1.0]])]});}
            var Q7;
            {var subQ2=sQuery(id+"F0.wireOp",EDGE,"E284");Q7=makeQuery(id+"F0.imprint","IMPRINT",FACE,{"disambiguationData":[TD([[makeQuery(id+"F0.imprint","IMPRINT",EDGE,{"derivedFrom":subQ2}),-1.0]])]});}
            var Q8;
            {var subQ5=sQuery(id+"F0.wireOp",EDGE,"E294");Q8=makeQuery(id+"F0.imprint","IMPRINT",FACE,{"disambiguationData":[TD([[makeQuery(id+"F0.imprint","IMPRINT",EDGE,{"derivedFrom":subQ5}),-1.0]])]});}
            var Q9;
            {var subQ5=sQuery(id+"F0.wireOp",EDGE,"E322");Q9=makeQuery(id+"F0.imprint","IMPRINT",FACE,{"disambiguationData":[TD([[makeQuery(id+"F0.imprint","IMPRINT",EDGE,{"derivedFrom":subQ5}),1.0]])]});}
            var Q10;
            {var subQ2=sQuery(id+"F0.wireOp",EDGE,"E312");Q10=makeQuery(id+"F0.imprint","IMPRINT",FACE,{"disambiguationData":[TD([[makeQuery(id+"F0.imprint","IMPRINT",EDGE,{"derivedFrom":subQ2}),1.0]])]});}
            var Q11;
            {var subQ9=sQuery(id+"F0.wireOp",EDGE,"E297");Q11=makeQuery(id+"F0.imprint","IMPRINT",FACE,{"disambiguationData":[TD([[makeQuery(id+"F0.imprint","IMPRINT",EDGE,{"derivedFrom":subQ9}),-1.0]])]});}
            var Q12;
            {var subQ0=sQuery(id+"F0.wireOp",EDGE,"E181");Q12=makeQuery(id+"F0.imprint","IMPRINT",FACE,{"disambiguationData":[TD([[makeQuery(id+"F0.imprint","IMPRINT",EDGE,{"derivedFrom":subQ0}),1.0]])]});}
            var Q13;
            {var subQ0=sQuery(id+"F0.wireOp",EDGE,"E243");Q13=makeQuery(id+"F0.imprint","IMPRINT",FACE,{"disambiguationData":[TD([[makeQuery(id+"F0.imprint","IMPRINT",EDGE,{"derivedFrom":subQ0}),-1.0]])]});}
            var Q14;
            {var subQ0=sQuery(id+"F0.wireOp",EDGE,"E271");Q14=makeQuery(id+"F0.imprint","IMPRINT",FACE,{"disambiguationData":[TD([[makeQuery(id+"F0.imprint","IMPRINT",EDGE,{"derivedFrom":subQ0}),1.0]])]});}
            var Q15;
            {var subQ0=sQuery(id+"F0.wireOp",EDGE,"E299");Q15=makeQuery(id+"F0.imprint","IMPRINT",FACE,{"disambiguationData":[TD([[makeQuery(id+"F0.imprint","IMPRINT",EDGE,{"derivedFrom":subQ0}),-1.0]])]});}
            extrude(context, id + "F2", {"entities" : qUnion([Q0, Q1, Q2, Q3, Q4, Q5, Q6, Q7, Q8, Q9, Q10, Q11, Q12, Q13, Q14, Q15]), "depth" : 50 * mm});
        }
    });
